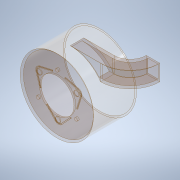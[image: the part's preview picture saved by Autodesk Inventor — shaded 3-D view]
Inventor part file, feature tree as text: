
AUTODESK INVENTOR PART (.ipt)
format: ipt  version: 2020 (Build 240168000, 168)  size: 289,280 bytes
history: native  units: in
note: dims shown in document units (in); Inventor stores cm internally (conversion verified against a paired STEP export)
features: sketch x9, extrude x6, projected_geometry x4, plane x2, shell x1, sweep x1, hole x1
ambient origin geometry x8: Origin, YZ Plane, XZ Plane, XY Plane, X Axis, Y Axis, Z Axis, Center Point
bodies: Solid1 (feature_tree)
feature tree (24):
  extrude  "Extrusion1"  Depth=3.1496in TaperAngle=0.0deg
  shell  "Shell1"  Thickness=0.1181in
  extrude  "Extrusion2"  Depth=3.1496in TaperAngle=0.0deg
  extrude  "Extrusion3"  Depth=1.5748in
  plane  "Work Plane1"
  extrude  "Extrusion4"  TaperAngle=120.0deg  [1 undecoded]
  extrude  "Extrusion5"  Depth=0.378in
  plane  "Work Plane4"
  sweep  "Sweep2"
  extrude  "Extrusion6"  [1 undecoded]
  hole  "Hole1"  [1 undecoded]
  sketch  "Sketch1"  dims[d1=5.3543in d2=3.1496in d3=0.0in d4=0.1181in]
  sketch  "Sketch2"  dims[d5=2.5197in d6=3.1496in d7=0.0in]
  sketch  "Sketch3"  dims[d8=0.378in d9=1.5748in]
  projected_geometry  "Projected Loop1"
  sketch  "Sketch4"  dims[d10=120.0deg d11=120.0deg]
  sketch  "Sketch6"  dims[d12=0.378in d13=0.378in]
  projected_geometry  "Projected Loop3"
  sketch  "Sketch9"  dims[d14=1.5748in d15=1.5748in]
  projected_geometry  "Projected Loop4"
  sketch  "Sketch10"  dims[d16=0.06in d17=0.0in d18=-0.9843in]
  sketch  "Sketch11"  dims[d24=1.1811in d25=0.9843in d26=0.0in]
  projected_geometry  "Projected Loop5"
  sketch  "Sketch14"  dims[d27=0.1181in d28=2.2201in d29=0.0in d37=0.0in d38=0.0in d39=0.0591in d40=0.0591in d41=0.0591in d42=0.0591in d43=0.0591in d44=0.0591in d45=0.0591in d46=0.9843in d47=0.9843in d48=0.9843in d49=0.9843in d50=0.9843in d51=0.9843in d52=0.0591in d53=0.0in d98=0.2362in d99=1.6142in d100=1.1811in d102=360.0deg d104=0.2362in d105=0.2362in d106=0.1575in d107=0.0787in d108=90.0deg d109=0.315in d110=0.8108in]
note: 3 required parameter values undecoded (feature->parameter linkage not recoverable at this tier; creation-order binding heuristic only, values carry confidence <= 0.55)
